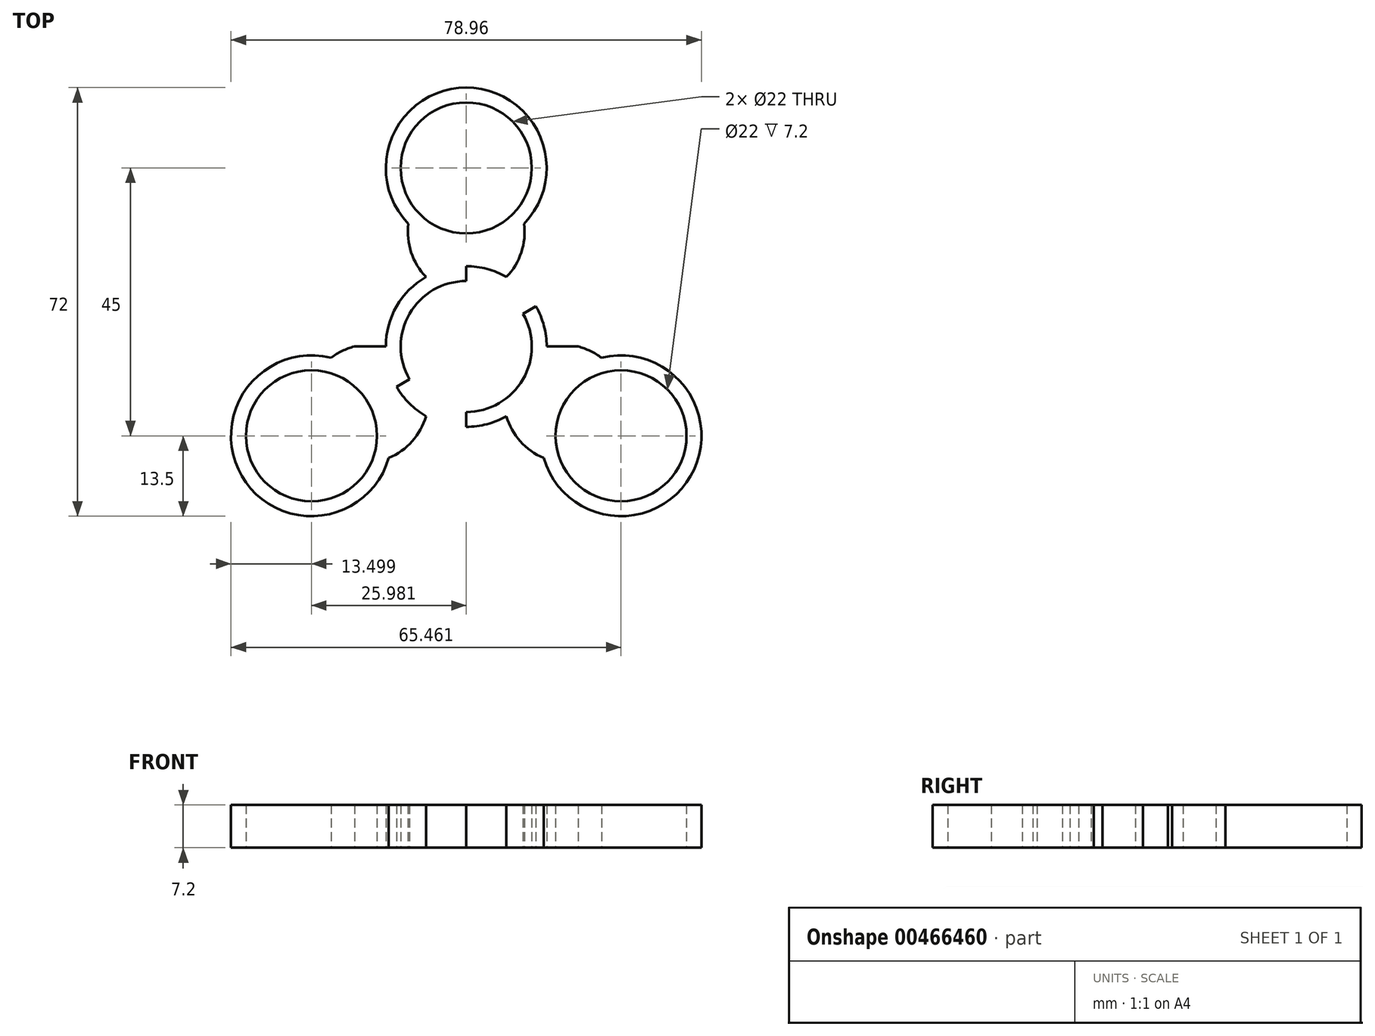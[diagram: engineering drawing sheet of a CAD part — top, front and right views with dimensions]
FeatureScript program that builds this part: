
annotation { "Feature Type Name" : "Feature", "Feature Type Description" : "" }
export const myFeature = defineFeature(function(context is Context, id is Id, definition is map)
    precondition{}
    {
        {
            var Q0;
            Q0=qCreatedBy(makeId("Top.planeOp"),FACE);
            var sketch = newSketch(context, id + "F0", { "sketchPlane" : qUnion([Q0])});
            skCircle(sketch, "E0", {"center": v(0, 0) * mm, "radius": 11 * mm});
            skCircle(sketch, "E1", {"center": v(0, 0) * mm, "radius": 13.5 * mm});
            skLineSegment(sketch, "E2", {"start": v(0, 0) * mm, "end": v(0, 30) * mm});
            skLineSegment(sketch, "E3.1.0", {"start": v(0, 0) * mm, "end": v(-25.98, -15) * mm});
            skLineSegment(sketch, "E3.2.0", {"start": v(0, 0) * mm, "end": v(25.98, -15) * mm});
            skCircle(sketch, "E4", {"center": v(0, 30) * mm, "radius": 11 * mm});
            skCircle(sketch, "E5", {"center": v(0, 30) * mm, "radius": 13.5 * mm});
            skCircle(sketch, "E6", {"center": v(-25.98, -15) * mm, "radius": 13.5 * mm});
            skCircle(sketch, "E7", {"center": v(-25.98, -15) * mm, "radius": 11 * mm});
            skCircle(sketch, "E8", {"center": v(25.98, -15) * mm, "radius": 11 * mm});
            skCircle(sketch, "E9", {"center": v(25.98, -15) * mm, "radius": 13.5 * mm});
            skLineSegment(sketch, "E10", {"start": v(0, 0) * mm, "end": v(-40.42, 0) * mm});
            skLineSegment(sketch, "E11", {"start": v(-40.42, 0) * mm, "end": v(44.58, 0) * mm});
            skLineSegment(sketch, "E12", {"start": v(0, 0) * mm, "end": v(0, -28.13) * mm});
            skLineSegment(sketch, "E13", {"start": v(0, 0) * mm, "end": v(35.38, 20.43) * mm});
            skLineSegment(sketch, "E14", {"start": v(35.38, 20.43) * mm, "end": v(0, 0) * mm});
            skLineSegment(sketch, "E15", {"start": v(0, 0) * mm, "end": v(-40.5, 23.39) * mm});
            skArc(sketch, "E16", {"start": v(-13.5, 0) * mm, "mid": v(-24.45, -3.58) * mm, "end": v(-25.98, -15) * mm});
            skArc(sketch, "E17.MirrorCS", {"start": v(-6.75, -11.7) * mm, "mid": v(-15.33, -19.39) * mm, "end": v(-25.98, -15) * mm});
            skArc(sketch, "E18.MirrorCS", {"start": v(6.75, -11.7) * mm, "mid": v(15.33, -19.39) * mm, "end": v(25.98, -15) * mm});
            skArc(sketch, "E19.MirrorCS", {"start": v(13.5, 0) * mm, "mid": v(24.45, -3.58) * mm, "end": v(25.98, -15) * mm});
            skArc(sketch, "E20.MirrorCS", {"start": v(-6.75, 11.7) * mm, "mid": v(-9.13, 22.97) * mm, "end": v(0, 30) * mm});
            skArc(sketch, "E21.MirrorCS", {"start": v(6.75, 11.7) * mm, "mid": v(9.13, 22.97) * mm, "end": v(0, 30) * mm});
            skSolve(sketch);
        }
        {
            var Q0;
            {var subQ0=sQuery(id+"F0.wireOp",EDGE,"E16");var subQ1=sQuery(id+"F0.wireOp",EDGE,"E6");var subQ2=makeQuery(id+"F0.imprint","INTERSECT",VERTEX,{"derivedFrom":[subQ1,subQ0]});Q0=makeQuery(id+"F0.imprint","IMPRINT",FACE,{"disambiguationData":[TD([[makeQuery(id+"F0.imprint","IMPRINT",EDGE,{"disambiguationData":[TD([[subQ2,-1.0]])],"derivedFrom":subQ1}),1.0]])]});}
            var Q1;
            {var subQ0=sQuery(id+"F0.wireOp",EDGE,"E17.MirrorCS");var subQ1=sQuery(id+"F0.wireOp",EDGE,"E1");var subQ2=makeQuery(id+"F0.imprint","INTERSECT",VERTEX,{"derivedFrom":[subQ1,subQ0]});Q1=makeQuery(id+"F0.imprint","IMPRINT",FACE,{"disambiguationData":[TD([[makeQuery(id+"F0.imprint","IMPRINT",EDGE,{"disambiguationData":[TD([[subQ2,1.0]])],"derivedFrom":subQ1}),-1.0]])]});}
            var Q2;
            {var subQ0=sQuery(id+"F0.wireOp",EDGE,"E16");var subQ5=sQuery(id+"F0.wireOp",EDGE,"E6");var subQ6=makeQuery(id+"F0.imprint","INTERSECT",VERTEX,{"derivedFrom":[subQ5,subQ0]});Q2=makeQuery(id+"F0.imprint","IMPRINT",FACE,{"disambiguationData":[TD([[makeQuery(id+"F0.imprint","IMPRINT",EDGE,{"disambiguationData":[TD([[subQ6,1.0]])],"derivedFrom":subQ5}),-1.0]])]});}
            var Q3;
            {var subQ0=sQuery(id+"F0.wireOp",EDGE,"E16");var subQ1=sQuery(id+"F0.wireOp",EDGE,"E6");var subQ2=makeQuery(id+"F0.imprint","INTERSECT",VERTEX,{"derivedFrom":[subQ1,subQ0]});Q3=makeQuery(id+"F0.imprint","IMPRINT",FACE,{"disambiguationData":[TD([[makeQuery(id+"F0.imprint","IMPRINT",EDGE,{"disambiguationData":[TD([[subQ2,1.0]])],"derivedFrom":subQ1}),1.0]])]});}
            var Q4;
            {var subQ0=sQuery(id+"F0.wireOp",EDGE,"E17.MirrorCS");var subQ1=sQuery(id+"F0.wireOp",EDGE,"E6");var subQ2=makeQuery(id+"F0.imprint","INTERSECT",VERTEX,{"derivedFrom":[subQ1,subQ0]});Q4=makeQuery(id+"F0.imprint","IMPRINT",FACE,{"disambiguationData":[TD([[makeQuery(id+"F0.imprint","IMPRINT",EDGE,{"disambiguationData":[TD([[subQ2,-1.0]])],"derivedFrom":subQ1}),1.0]])]});}
            var Q5;
            {var subQ0=sQuery(id+"F0.wireOp",EDGE,"E9");var subQ1=sQuery(id+"F0.wireOp",EDGE,"E3.2.0");var subQ2=makeQuery(id+"F0.imprint","INTERSECT",VERTEX,{"derivedFrom":[subQ1,subQ0]});Q5=makeQuery(id+"F0.imprint","IMPRINT",FACE,{"disambiguationData":[TD([[makeQuery(id+"F0.imprint","IMPRINT",EDGE,{"disambiguationData":[TD([[subQ2,-1.0]])],"derivedFrom":subQ1}),-1.0]])]});}
            var Q6;
            {var subQ0=sQuery(id+"F0.wireOp",EDGE,"E18.MirrorCS");var subQ1=sQuery(id+"F0.wireOp",EDGE,"E1");var subQ2=makeQuery(id+"F0.imprint","INTERSECT",VERTEX,{"derivedFrom":[subQ1,subQ0]});Q6=makeQuery(id+"F0.imprint","IMPRINT",FACE,{"disambiguationData":[TD([[makeQuery(id+"F0.imprint","IMPRINT",EDGE,{"disambiguationData":[TD([[subQ2,-1.0]])],"derivedFrom":subQ1}),-1.0]])]});}
            var Q7;
            {var subQ2=sQuery(id+"F0.wireOp",EDGE,"E1");var subQ7=sQuery(id+"F0.wireOp",EDGE,"E3.2.0");var subQ9=makeQuery(id+"F0.imprint","INTERSECT",VERTEX,{"derivedFrom":[subQ2,subQ7]});Q7=makeQuery(id+"F0.imprint","IMPRINT",FACE,{"disambiguationData":[TD([[makeQuery(id+"F0.imprint","IMPRINT",EDGE,{"disambiguationData":[TD([[subQ9,-1.0]])],"derivedFrom":subQ7}),1.0]])]});}
            var Q8;
            {var subQ0=sQuery(id+"F0.wireOp",EDGE,"E19.MirrorCS");var subQ1=sQuery(id+"F0.wireOp",EDGE,"E8");var subQ2=makeQuery(id+"F0.imprint","INTERSECT",VERTEX,{"derivedFrom":[subQ1,subQ0]});Q8=makeQuery(id+"F0.imprint","IMPRINT",FACE,{"disambiguationData":[TD([[makeQuery(id+"F0.imprint","IMPRINT",EDGE,{"disambiguationData":[TD([[subQ2,1.0]])],"derivedFrom":subQ1}),-1.0]])]});}
            var Q9;
            {var subQ0=sQuery(id+"F0.wireOp",EDGE,"E9");var subQ1=sQuery(id+"F0.wireOp",EDGE,"E3.2.0");var subQ2=makeQuery(id+"F0.imprint","INTERSECT",VERTEX,{"derivedFrom":[subQ1,subQ0]});Q9=makeQuery(id+"F0.imprint","IMPRINT",FACE,{"disambiguationData":[TD([[makeQuery(id+"F0.imprint","IMPRINT",EDGE,{"disambiguationData":[TD([[subQ2,-1.0]])],"derivedFrom":subQ1}),1.0]])]});}
            var Q10;
            {var subQ4=sQuery(id+"F0.wireOp",EDGE,"E0");var subQ6=sQuery(id+"F0.wireOp",EDGE,"E14");var subQ8=makeQuery(id+"F0.imprint","INTERSECT",VERTEX,{"derivedFrom":[subQ4,subQ6]});Q10=makeQuery(id+"F0.imprint","IMPRINT",FACE,{"disambiguationData":[TD([[makeQuery(id+"F0.imprint","IMPRINT",EDGE,{"disambiguationData":[TD([[subQ8,-1.0]])],"derivedFrom":subQ4}),-1.0]])]});}
            var Q11;
            {var subQ0=sQuery(id+"F0.wireOp",EDGE,"E14");var subQ1=sQuery(id+"F0.wireOp",EDGE,"E0");var subQ2=makeQuery(id+"F0.imprint","INTERSECT",VERTEX,{"derivedFrom":[subQ1,subQ0]});Q11=makeQuery(id+"F0.imprint","IMPRINT",FACE,{"disambiguationData":[TD([[makeQuery(id+"F0.imprint","IMPRINT",EDGE,{"disambiguationData":[TD([[subQ2,1.0]])],"derivedFrom":subQ1}),-1.0]])]});}
            var Q12;
            {var subQ0=sQuery(id+"F0.wireOp",EDGE,"E11");var subQ1=sQuery(id+"F0.wireOp",EDGE,"E0");var subQ2=makeQuery(id+"F0.imprint","INTERSECT",VERTEX,{"disambiguationData":[OD(0.0)],"derivedFrom":[subQ1,subQ0]});Q12=makeQuery(id+"F0.imprint","IMPRINT",FACE,{"disambiguationData":[TD([[makeQuery(id+"F0.imprint","IMPRINT",EDGE,{"disambiguationData":[TD([[subQ2,1.0]])],"derivedFrom":subQ1}),-1.0]])]});}
            var Q13;
            {var subQ4=sQuery(id+"F0.wireOp",EDGE,"E12");var subQ6=sQuery(id+"F0.wireOp",EDGE,"E0");var subQ7=makeQuery(id+"F0.imprint","INTERSECT",VERTEX,{"derivedFrom":[subQ6,subQ4]});Q13=makeQuery(id+"F0.imprint","IMPRINT",FACE,{"disambiguationData":[TD([[makeQuery(id+"F0.imprint","IMPRINT",EDGE,{"disambiguationData":[TD([[subQ7,-1.0]])],"derivedFrom":subQ6}),-1.0]])]});}
            var Q14;
            {var subQ4=sQuery(id+"F0.wireOp",EDGE,"E3.1.0");var subQ5=sQuery(id+"F0.wireOp",EDGE,"E0");var subQ6=makeQuery(id+"F0.imprint","INTERSECT",VERTEX,{"derivedFrom":[subQ5,subQ4]});Q14=makeQuery(id+"F0.imprint","IMPRINT",FACE,{"disambiguationData":[TD([[makeQuery(id+"F0.imprint","IMPRINT",EDGE,{"disambiguationData":[TD([[subQ6,-1.0]])],"derivedFrom":subQ5}),-1.0]])]});}
            var Q15;
            {var subQ0=sQuery(id+"F0.wireOp",EDGE,"E11");var subQ1=sQuery(id+"F0.wireOp",EDGE,"E0");var subQ2=makeQuery(id+"F0.imprint","INTERSECT",VERTEX,{"disambiguationData":[OD(1.0)],"derivedFrom":[subQ1,subQ0]});Q15=makeQuery(id+"F0.imprint","IMPRINT",FACE,{"disambiguationData":[TD([[makeQuery(id+"F0.imprint","IMPRINT",EDGE,{"disambiguationData":[TD([[subQ2,-1.0]])],"derivedFrom":subQ1}),-1.0]])]});}
            var Q16;
            {var subQ0=sQuery(id+"F0.wireOp",EDGE,"E15");var subQ1=sQuery(id+"F0.wireOp",EDGE,"E0");var subQ2=makeQuery(id+"F0.imprint","INTERSECT",VERTEX,{"derivedFrom":[subQ1,subQ0]});Q16=makeQuery(id+"F0.imprint","IMPRINT",FACE,{"disambiguationData":[TD([[makeQuery(id+"F0.imprint","IMPRINT",EDGE,{"disambiguationData":[TD([[subQ2,-1.0]])],"derivedFrom":subQ1}),-1.0]])]});}
            var Q17;
            {var subQ0=sQuery(id+"F0.wireOp",EDGE,"E2");var subQ1=sQuery(id+"F0.wireOp",EDGE,"E0");var subQ2=makeQuery(id+"F0.imprint","INTERSECT",VERTEX,{"derivedFrom":[subQ1,subQ0]});Q17=makeQuery(id+"F0.imprint","IMPRINT",FACE,{"disambiguationData":[TD([[makeQuery(id+"F0.imprint","IMPRINT",EDGE,{"disambiguationData":[TD([[subQ2,-1.0]])],"derivedFrom":subQ1}),-1.0]])]});}
            var Q18;
            {var subQ0=sQuery(id+"F0.wireOp",EDGE,"E20.MirrorCS");var subQ1=sQuery(id+"F0.wireOp",EDGE,"E1");var subQ2=makeQuery(id+"F0.imprint","INTERSECT",VERTEX,{"derivedFrom":[subQ1,subQ0]});Q18=makeQuery(id+"F0.imprint","IMPRINT",FACE,{"disambiguationData":[TD([[makeQuery(id+"F0.imprint","IMPRINT",EDGE,{"disambiguationData":[TD([[subQ2,1.0]])],"derivedFrom":subQ1}),-1.0]])]});}
            var Q19;
            {var subQ0=sQuery(id+"F0.wireOp",EDGE,"E21.MirrorCS");var subQ1=sQuery(id+"F0.wireOp",EDGE,"E1");var subQ2=makeQuery(id+"F0.imprint","INTERSECT",VERTEX,{"derivedFrom":[subQ1,subQ0]});Q19=makeQuery(id+"F0.imprint","IMPRINT",FACE,{"disambiguationData":[TD([[makeQuery(id+"F0.imprint","IMPRINT",EDGE,{"disambiguationData":[TD([[subQ2,-1.0]])],"derivedFrom":subQ1}),-1.0]])]});}
            var Q20;
            {var subQ0=sQuery(id+"F0.wireOp",EDGE,"E5");var subQ1=sQuery(id+"F0.wireOp",EDGE,"E2");var subQ2=makeQuery(id+"F0.imprint","INTERSECT",VERTEX,{"derivedFrom":[subQ1,subQ0]});Q20=makeQuery(id+"F0.imprint","IMPRINT",FACE,{"disambiguationData":[TD([[makeQuery(id+"F0.imprint","IMPRINT",EDGE,{"disambiguationData":[TD([[subQ2,-1.0]])],"derivedFrom":subQ1}),-1.0]])]});}
            var Q21;
            {var subQ0=sQuery(id+"F0.wireOp",EDGE,"E5");var subQ1=sQuery(id+"F0.wireOp",EDGE,"E2");var subQ2=makeQuery(id+"F0.imprint","INTERSECT",VERTEX,{"derivedFrom":[subQ1,subQ0]});Q21=makeQuery(id+"F0.imprint","IMPRINT",FACE,{"disambiguationData":[TD([[makeQuery(id+"F0.imprint","IMPRINT",EDGE,{"disambiguationData":[TD([[subQ2,-1.0]])],"derivedFrom":subQ1}),1.0]])]});}
            var Q22;
            {var subQ0=sQuery(id+"F0.wireOp",EDGE,"E20.MirrorCS");var subQ1=sQuery(id+"F0.wireOp",EDGE,"E4");var subQ2=makeQuery(id+"F0.imprint","INTERSECT",VERTEX,{"derivedFrom":[subQ1,subQ0]});Q22=makeQuery(id+"F0.imprint","IMPRINT",FACE,{"disambiguationData":[TD([[makeQuery(id+"F0.imprint","IMPRINT",EDGE,{"disambiguationData":[TD([[subQ2,1.0]])],"derivedFrom":subQ1}),-1.0]])]});}
            extrude(context, id + "F1", {"entities" : qUnion([Q0, Q1, Q2, Q3, Q4, Q5, Q6, Q7, Q8, Q9, Q10, Q11, Q12, Q13, Q14, Q15, Q16, Q17, Q18, Q19, Q20, Q21, Q22]), "depth" : 7.2 * mm});
        }
    });
